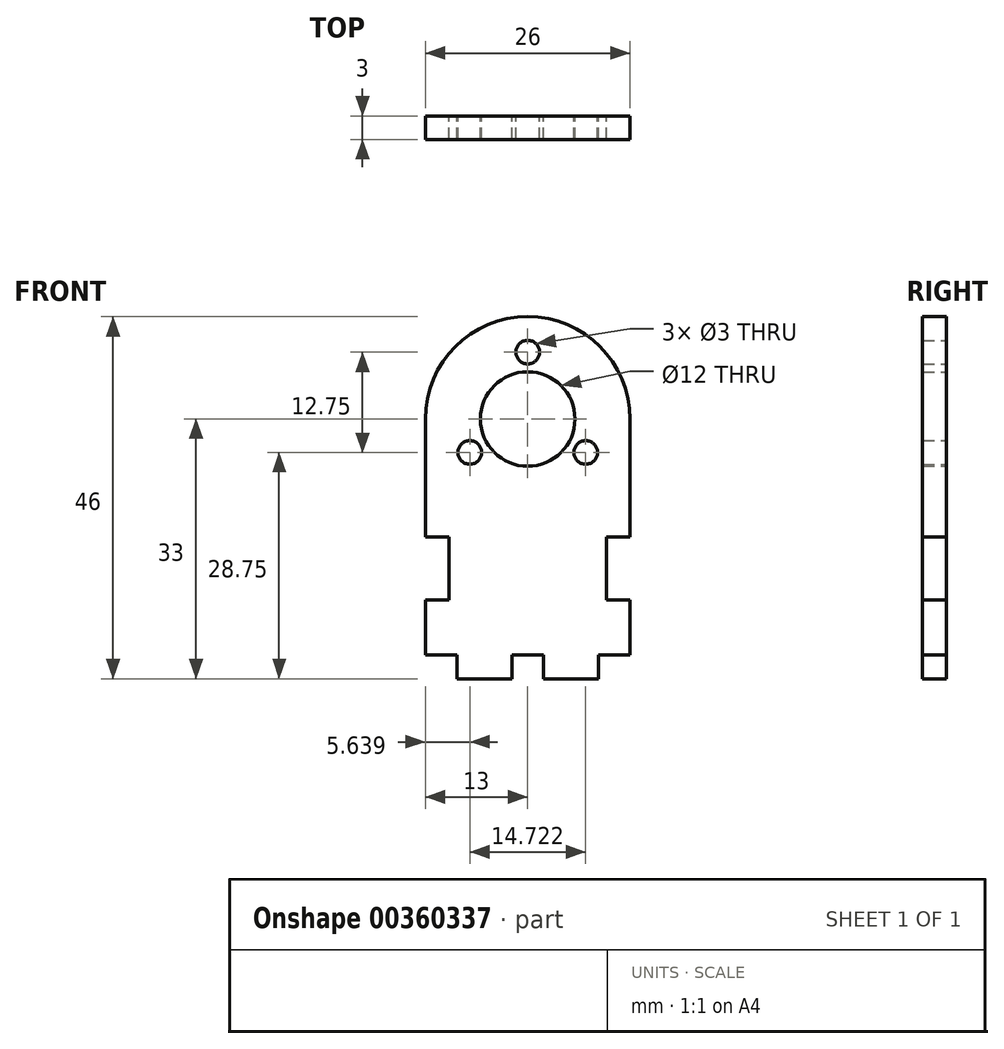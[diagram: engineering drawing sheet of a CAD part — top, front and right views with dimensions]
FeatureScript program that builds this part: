
annotation { "Feature Type Name" : "Feature", "Feature Type Description" : "" }
export const myFeature = defineFeature(function(context is Context, id is Id, definition is map)
    precondition{}
    {
        {
            var Q0;
            Q0=qCreatedBy(makeId("Front.planeOp"),FACE);
            var sketch = newSketch(context, id + "F0", { "sketchPlane" : qUnion([Q0])});
            skArc(sketch, "E0", {"start": v(13, 30) * mm, "mid": v(0, 43) * mm, "end": v(-13, 30) * mm});
            skLineSegment(sketch, "E1.bottom", {"start": v(-13, 30) * mm, "end": v(13, 30) * mm, "construction": true});
            skLineSegment(sketch, "E1.left", {"start": v(-13, 30) * mm, "end": v(-13, 0) * mm, "construction": true});
            skLineSegment(sketch, "E1.right", {"start": v(13, 30) * mm, "end": v(13, 0) * mm, "construction": true});
            skCircle(sketch, "E2", {"center": v(0, 38.5) * mm, "radius": 1.5 * mm});
            skCircle(sketch, "E3.1.0", {"center": v(-7.36, 25.75) * mm, "radius": 1.5 * mm});
            skCircle(sketch, "E3.2.0", {"center": v(7.36, 25.75) * mm, "radius": 1.5 * mm});
            skLineSegment(sketch, "E4", {"start": v(-13, 0) * mm, "end": v(-9, 0) * mm});
            skLineSegment(sketch, "E5", {"start": v(-9, 0) * mm, "end": v(-9, -3) * mm});
            skLineSegment(sketch, "E6", {"start": v(-9, -3) * mm, "end": v(-2, -3) * mm});
            skLineSegment(sketch, "E7", {"start": v(-2, -3) * mm, "end": v(-2, 0) * mm});
            skLineSegment(sketch, "E8", {"start": v(-2, 0) * mm, "end": v(0, 0) * mm});
            skLineSegment(sketch, "E9.MirrorCS", {"start": v(2, 0) * mm, "end": v(0, 0) * mm});
            skLineSegment(sketch, "E10.MirrorCS", {"start": v(2, -3) * mm, "end": v(2, 0) * mm});
            skLineSegment(sketch, "E11.MirrorCS", {"start": v(13, 0) * mm, "end": v(9, 0) * mm});
            skLineSegment(sketch, "E12.MirrorCS", {"start": v(9, -3) * mm, "end": v(2, -3) * mm});
            skLineSegment(sketch, "E13.MirrorCS", {"start": v(9, 0) * mm, "end": v(9, -3) * mm});
            skCircle(sketch, "E14", {"center": v(0, 30) * mm, "radius": 6 * mm});
            skLineSegment(sketch, "E15", {"start": v(-13, 30) * mm, "end": v(-13, 15) * mm});
            skLineSegment(sketch, "E16", {"start": v(-13, 15) * mm, "end": v(-10, 15) * mm});
            skLineSegment(sketch, "E17", {"start": v(-10, 15) * mm, "end": v(-10, 7) * mm});
            skLineSegment(sketch, "E18", {"start": v(-10, 7) * mm, "end": v(-13, 7) * mm});
            skLineSegment(sketch, "E19", {"start": v(-13, 7) * mm, "end": v(-13, 0) * mm});
            skLineSegment(sketch, "E20", {"start": v(13, 30) * mm, "end": v(13, 15) * mm});
            skLineSegment(sketch, "E21", {"start": v(13, 15) * mm, "end": v(10, 15) * mm});
            skLineSegment(sketch, "E22", {"start": v(10, 15) * mm, "end": v(10, 7) * mm});
            skLineSegment(sketch, "E23", {"start": v(10, 7) * mm, "end": v(13, 7) * mm});
            skLineSegment(sketch, "E24", {"start": v(13, 7) * mm, "end": v(13, 0) * mm});
            skSolve(sketch);
        }
        {
            var Q0;
            Q0=makeQuery(id+"F0.imprint","IMPRINT",FACE,{"disambiguationData":[TD([[makeQuery(id+"F0.imprint","IMPRINT",EDGE,{"derivedFrom":sQuery(id+"F0.wireOp",EDGE,"E0")}),1.0]])]});
            extrude(context, id + "F1", {"entities" : qUnion([Q0]), "depth" : 3 * mm});
        }
    });
